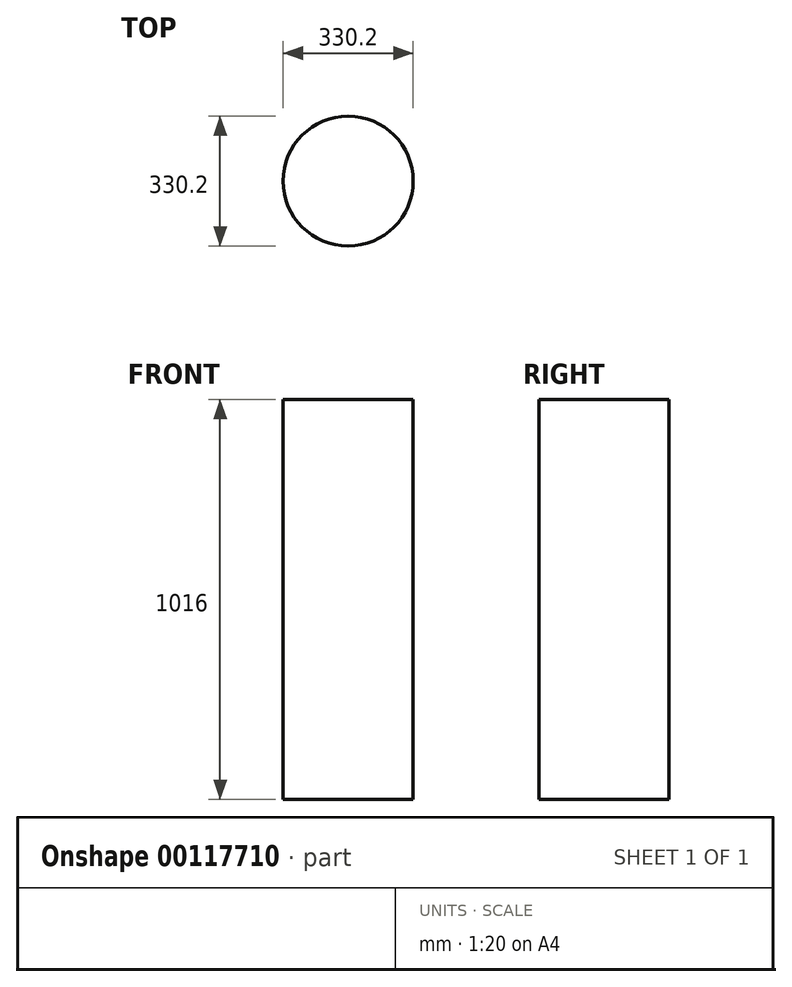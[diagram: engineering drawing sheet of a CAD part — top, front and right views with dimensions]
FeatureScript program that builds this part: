
annotation { "Feature Type Name" : "Feature", "Feature Type Description" : "" }
export const myFeature = defineFeature(function(context is Context, id is Id, definition is map)
    precondition{}
    {
        {
            var Q0;
            Q0=qCreatedBy(makeId("Top.planeOp"),FACE);
            var sketch = newSketch(context, id + "F0", { "sketchPlane" : qUnion([Q0])});
            skCircle(sketch, "E0", {"center": v(0, 0) * mm, "radius": 165.1 * mm});
            skSolve(sketch);
        }
        {
            var Q0;
            Q0 = qSketchRegion(id + "F0", true);
            extrude(context, id + "F1", {"entities" : qUnion([Q0]), "depth" : 1016 * mm});
        }
    });
